# Revit family: 63_UN_LEDPanel_LPS-P 120x30_Norton
name_source: partatom
category: Lighting Fixtures
units: mm (PartAtom-declared; Revit-internal decimal feet)

## family parameters
Always vertical = Yes
Cut with Voids When Loaded = No
Light Source = Yes
OmniClass Number = 23.80.70.11.14.11
OmniClass Title = Downlights
Part Type = Normal
Room Calculation Point = Yes
Round Connector Dimension = Use Diameter
Shared = No
Work Plane-Based = No

## types (3) — shared parameters
Apparent Load = 32 VA
Assembly Code = 63.0
Calc_L1_Symbol = 12 mm  [stored 0.0393701 ft]
Calc_L2_Symbol = 3 mm  [stored 0.00984252 ft]
Color Filter = 16777215
Dimming Lamp Color Temperature Shift = <None>
ETIM Code = -
Emit Shape Visible in Rendering = No
Emit from Rectangle Length = 1156 mm  [stored 3.79265 ft]
Emit from Rectangle Width = 256 mm  [stored 0.839895 ft]
GTIN Code = -
H1 = 14 mm  [stored 0.0459318 ft]
Housing_Material = Select RGB Value for different appearance
IK Value = IK06
IP Value = IP20
ISBN Code = -
IfcExportAs = IfcLightFixtureType
IfcExportType = USERDEFINED
L1 = 1196 mm  [stored 3.92388 ft]
L2 = 296 mm  [stored 0.971129 ft]
L3 = 20 mm  [stored 0.0656168 ft]
L4 = 1100 mm
LED Panel = Yes
Lamp = LED
Manufacturer = Norton
Model = LPS
Tilt Angle = 90.00°
Type Comments = LPS-P
URL = https://www.ivlibrary.com
Voltage = 230 V
Wattage Comments = 32

## per-type parameters (varying)
| type | Luminous Flux (lm) | Photometric Web File |
| LPS-P 865 3500LM 120X30 | 3500 lm | LPS-P 865 3500LM 120X30_LDT.ies |
| LPS-P 84 3400LM 120X30 | 3400 lm | LPS-P 84 3400LM 120X30_LDT.ies |
| LPS-P 83 3200LM 120X30 | 3200 lm | LPS-P 83 3200LM 120X30_LDT.ies |

note: [stored X ft] marks values corroborated as IEEE doubles in the binary element streams (Revit-internal decimal feet)

## geometry (parser evidence)
native form markers: Sweep x2
no freeform markers — native parametric forms only
